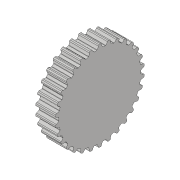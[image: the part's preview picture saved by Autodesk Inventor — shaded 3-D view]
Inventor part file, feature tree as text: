
AUTODESK INVENTOR PART (.ipt)
format: ipt  version: 2019.4 (Build 234330000, 330)  size: 334,848 bytes
history: native  units: mm
features: fillet x2, other x1, extrude x1, pattern_circular x1, sketch x1
ambient origin geometry x8: Origin, YZ Plane, XZ Plane, XY Plane, X Axis, Y Axis, Z Axis, Center Point
bodies: Body1 (feature_tree)
feature tree (6):
  other  "ソリッド1"
  extrude  "押し出し1"  Depth=1.95mm
  fillet  "フィレット1"  Radius=1.975mm
  fillet  "フィレット2"  Radius=1.11mm
  pattern_circular  "円形状パターン1"  [2 undecoded]
  sketch  "スケッチ1"
note: 2 required parameter values undecoded (feature->parameter linkage not recoverable at this tier; creation-order binding heuristic only, values carry confidence <= 0.55)
